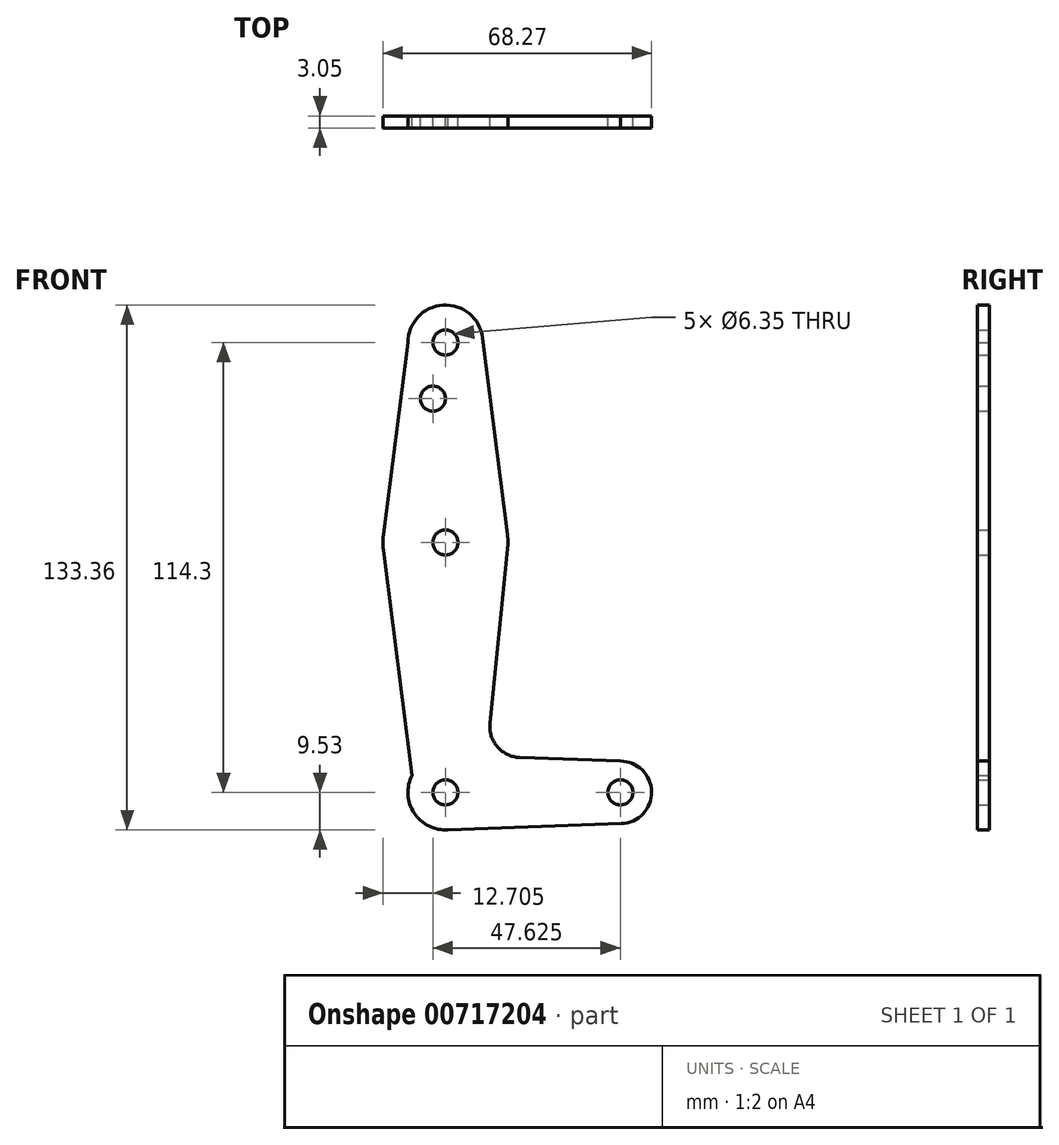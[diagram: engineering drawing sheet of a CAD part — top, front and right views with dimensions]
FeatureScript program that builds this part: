
annotation { "Feature Type Name" : "Feature", "Feature Type Description" : "" }
export const myFeature = defineFeature(function(context is Context, id is Id, definition is map)
    precondition{}
    {
        {
            var Q0;
            Q0=qCreatedBy(makeId("Front.planeOp"),FACE);
            var sketch = newSketch(context, id + "F0", { "sketchPlane" : qUnion([Q0])});
            skLineSegment(sketch, "E0", {"start": v(0, 0) * mm, "end": v(0, 114.3) * mm});
            skLineSegment(sketch, "E1", {"start": v(0, 0) * mm, "end": v(44.45, 0) * mm});
            skCircle(sketch, "E2", {"center": v(0, 114.3) * mm, "radius": 9.53 * mm});
            skCircle(sketch, "E3", {"center": v(0, 63.5) * mm, "radius": 15.88 * mm});
            skCircle(sketch, "E4", {"center": v(0, 0) * mm, "radius": 9.53 * mm});
            skCircle(sketch, "E5", {"center": v(44.45, 0) * mm, "radius": 7.94 * mm});
            skLineSegment(sketch, "E6", {"start": v(-9.53, 114.3) * mm, "end": v(-15.75, 65.5) * mm});
            skLineSegment(sketch, "E7", {"start": v(0, -9.52) * mm, "end": v(44.73, -7.93) * mm});
            skLineSegment(sketch, "E8", {"start": v(44.45, 7.94) * mm, "end": v(18.93, 8.85) * mm});
            skLineSegment(sketch, "E9", {"start": v(11.3, 17.6) * mm, "end": v(15.8, 61.9) * mm});
            skLineSegment(sketch, "E10", {"start": v(15.75, 65.48) * mm, "end": v(9.45, 115.5) * mm});
            skLineSegment(sketch, "E11", {"start": v(-15.75, 61.5) * mm, "end": v(-8.46, 4.37) * mm});
            skCircle(sketch, "E12", {"center": v(0, 114.3) * mm, "radius": 3.18 * mm});
            skCircle(sketch, "E13", {"center": v(-3.18, 100.03) * mm, "radius": 3.18 * mm});
            skCircle(sketch, "E14", {"center": v(44.45, 0) * mm, "radius": 3.18 * mm});
            skCircle(sketch, "E15", {"center": v(0, 0) * mm, "radius": 3.18 * mm});
            skCircle(sketch, "E16", {"center": v(0, 63.5) * mm, "radius": 3.18 * mm});
            skArc(sketch, "E17.filletArc", {"start": v(11.3, 17.6) * mm, "mid": v(13.22, 11.57) * mm, "end": v(18.93, 8.85) * mm});
            skSolve(sketch);
        }
        {
            var Q0;
            Q0 = qSketchRegion(id + "F0", true);
            var Q1;
            {var subQ0=sQuery(id+"F0.wireOp",EDGE,"E15");var subQ1=sQuery(id+"F0.wireOp",EDGE,"E0");var subQ2=makeQuery(id+"F0.imprint","INTERSECT",VERTEX,{"derivedFrom":[subQ1,subQ0]});Q1=makeQuery(id+"F0.imprint","IMPRINT",FACE,{"disambiguationData":[TD([[makeQuery(id+"F0.imprint","IMPRINT",EDGE,{"disambiguationData":[TD([[subQ2,-1.0]])],"derivedFrom":subQ1}),-1.0]])]});}
            extrude(context, id + "F1", {"entities" : qUnion([Q0, Q1]), "depth" : 3.05 * mm, "offsetDistance" : 25.4 * mm});
        }
    });
